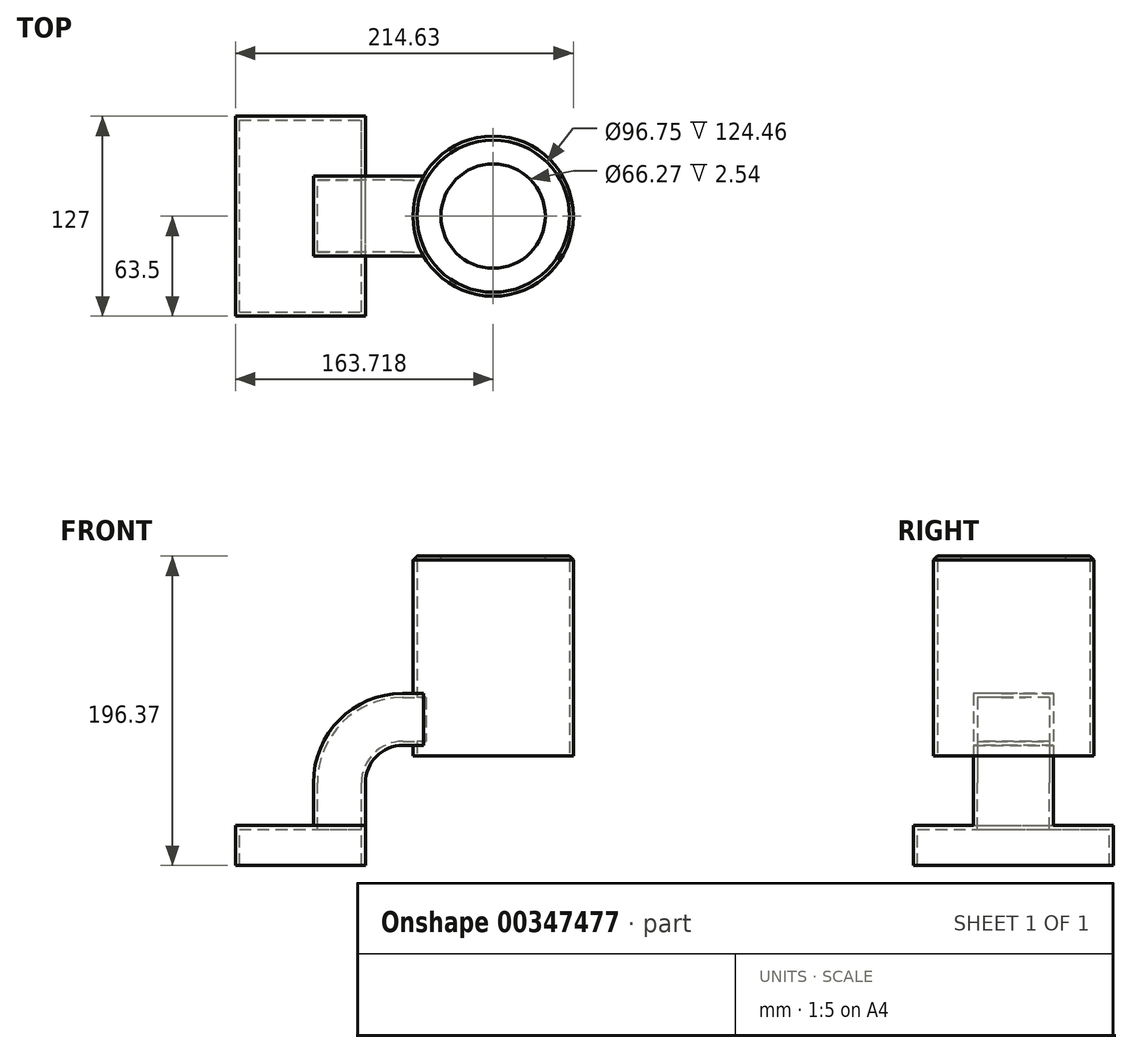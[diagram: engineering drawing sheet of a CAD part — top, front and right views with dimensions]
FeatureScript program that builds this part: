
annotation { "Feature Type Name" : "Feature", "Feature Type Description" : "" }
export const myFeature = defineFeature(function(context is Context, id is Id, definition is map)
    precondition{}
    {
        {
            var Q0;
            Q0=qCreatedBy(makeId("Front.planeOp"),FACE);
            var sketch = newSketch(context, id + "F0", { "sketchPlane" : qUnion([Q0])});
            skLineSegment(sketch, "E0.bottom", {"start": v(-41.65, -6.6) * mm, "end": v(40.9, -6.6) * mm});
            skLineSegment(sketch, "E0.top", {"start": v(-41.65, 18.8) * mm, "end": v(40.9, 18.8) * mm});
            skLineSegment(sketch, "E0.left", {"start": v(-41.65, -6.6) * mm, "end": v(-41.65, 18.8) * mm});
            skLineSegment(sketch, "E0.right", {"start": v(40.9, -6.6) * mm, "end": v(40.9, 18.8) * mm});
            skLineSegment(sketch, "E1.bottom", {"start": v(71.38, 62.77) * mm, "end": v(172.98, 62.77) * mm});
            skLineSegment(sketch, "E1.top", {"start": v(71.38, 189.77) * mm, "end": v(172.98, 189.77) * mm});
            skLineSegment(sketch, "E1.left", {"start": v(71.38, 62.77) * mm, "end": v(71.38, 189.77) * mm});
            skLineSegment(sketch, "E1.right", {"start": v(172.98, 62.77) * mm, "end": v(172.98, 189.77) * mm});
            skLineSegment(sketch, "E2", {"start": v(40.9, 18.8) * mm, "end": v(40.9, 45.75) * mm});
            skArc(sketch, "E3", {"start": v(40.9, 45.75) * mm, "mid": v(47.89, 62.61) * mm, "end": v(64.75, 69.6) * mm});
            skLineSegment(sketch, "E4", {"start": v(64.75, 69.6) * mm, "end": v(122.07, 69.6) * mm});
            skLineSegment(sketch, "E5.0", {"start": v(64.75, 102.62) * mm, "end": v(122.07, 102.62) * mm});
            skArc(sketch, "E5.1", {"start": v(7.88, 45.75) * mm, "mid": v(24.54, 85.96) * mm, "end": v(64.75, 102.62) * mm});
            skLineSegment(sketch, "E5.2", {"start": v(7.88, 18.8) * mm, "end": v(7.88, 45.75) * mm});
            skLineSegment(sketch, "E6", {"start": v(122.07, 69.6) * mm, "end": v(122.07, 102.62) * mm});
            skFitSpline(sketch, "E7", {"points": [v(-41.65, 18.8) * mm, v(64.75, 102.62) * mm], "startDerivative": vector(-1.45, 45.26) * mm, "endDerivative": vector(278.29, 0.6) * mm});
            skLineSegment(sketch, "E8", {"start": v(122.07, 62.77) * mm, "end": v(122.07, 189.77) * mm});
            skSolve(sketch);
        }
        {
            var Q0;
            Q0=makeQuery(id+"F0.imprint","IMPRINT",FACE,{"disambiguationData":[TD([[makeQuery(id+"F0.imprint","IMPRINT",EDGE,{"derivedFrom":sQuery(id+"F0.wireOp",EDGE,"E0.bottom")}),1.0]])]});
            extrude(context, id + "F1", {"entities" : qUnion([Q0]), "endBound" : BoundingType.SYMMETRIC, "depth" : 127 * mm});
        }
        {
            var Q0;
            {var subQ0=sQuery(id+"F0.wireOp",EDGE,"E2");Q0=makeQuery(id+"F0.imprint","IMPRINT",FACE,{"disambiguationData":[TD([[makeQuery(id+"F0.imprint","IMPRINT",EDGE,{"derivedFrom":subQ0}),1.0]])]});}
            var Q1;
            {var subQ5=sQuery(id+"F0.wireOp",EDGE,"E6");Q1=makeQuery(id+"F0.imprint","IMPRINT",FACE,{"disambiguationData":[TD([[makeQuery(id+"F0.imprint","IMPRINT",EDGE,{"derivedFrom":subQ5}),1.0]])]});}
            var Q2;
            {var subQ0=sQuery(id+"F0.wireOp",EDGE,"E4");var subQ1=sQuery(id+"F0.wireOp",EDGE,"E1.left");var subQ2=makeQuery(id+"F0.imprint","INTERSECT",VERTEX,{"derivedFrom":[subQ1,subQ0]});Q2=makeQuery(id+"F0.imprint","IMPRINT",FACE,{"disambiguationData":[TD([[makeQuery(id+"F0.imprint","IMPRINT",EDGE,{"disambiguationData":[TD([[subQ2,-1.0]])],"derivedFrom":subQ1}),-1.0]])]});}
            extrude(context, id + "F2", {"entities" : qUnion([Q0, Q1, Q2]), "operationType" : NewBodyOperationType.ADD, "endBound" : BoundingType.SYMMETRIC, "depth" : 50.8 * mm});
        }
        {
            var Q0;
            {var subQ4=sQuery(id+"F0.wireOp",EDGE,"E5.1");Q0=makeQuery(id+"F0.imprint","IMPRINT",FACE,{"disambiguationData":[TD([[makeQuery(id+"F0.imprint","IMPRINT",EDGE,{"derivedFrom":subQ4}),1.0]])]});}
            extrude(context, id + "F3", {"entities" : qUnion([Q0]), "operationType" : NewBodyOperationType.ADD, "endBound" : BoundingType.SYMMETRIC, "depth" : 15.24 * mm});
        }
        {
            var Q0;
            {var subQ0=sQuery(id+"F0.wireOp",EDGE,"E1.right");Q0=makeQuery(id+"F0.imprint","IMPRINT",FACE,{"disambiguationData":[TD([[makeQuery(id+"F0.imprint","IMPRINT",EDGE,{"derivedFrom":subQ0}),1.0]])]});}
            var Q1;
            Q1=sQuery(id+"F0.wireOp",EDGE,"E8");
            revolve(context, id + "F4", {"operationType" : NewBodyOperationType.ADD, "entities" : qUnion([Q0]), "axis" : qUnion([Q1]), "revolveType" : RevolveType.FULL});
        }
        {
            var Q0;
            Q0=makeQuery(id+"F1.opExtrude","SWEPT_FACE",FACE,{"disambiguationData":[OSD([sQuery(id+"F0.wireOp",EDGE,"E0.bottom")])]});
            var Q1;
            Q1=makeQuery(id+"F4.opRevolve","SWEPT_FACE",FACE,{"disambiguationData":[OSD([sQuery(id+"F0.wireOp",EDGE,"E1.bottom")])]});
            shell(context, id + "F5", {"entities" : qUnion([Q0, Q1]), "thickness" : 2.54 * mm});
        }
        {
            var Q0;
            Q0=makeQuery(id+"F4.opRevolve","SWEPT_EDGE",EDGE,{"disambiguationData":[OSD([sQuery(id+"F0.wireOp",EDGE,"E1.top"),sQuery(id+"F0.wireOp",EDGE,"E1.right")])]});
            chamfer(context, id + "F6", {"entities" : qUnion([Q0]), "width" : 2.54 * mm, "tangentPropagation" : true});
        }
        {
            var Q0;
            Q0=makeQuery(id+"F4.opRevolve","SWEPT_FACE",FACE,{"disambiguationData":[OSD([sQuery(id+"F0.wireOp",EDGE,"E1.top")])]});
            var sketch = newSketch(context, id + "F7", { "sketchPlane" : qUnion([Q0])});
            skCircle(sketch, "E9", {"center": v(122.07, 0) * mm, "radius": 33.14 * mm});
            skSolve(sketch);
        }
        {
            var Q0;
            Q0=makeQuery(id+"F7.imprint","IMPRINT",FACE,{"disambiguationData":[TD([[makeQuery(id+"F7.imprint","IMPRINT",EDGE,{"derivedFrom":sQuery(id+"F7.wireOp",EDGE,"E9")}),1.0]])]});
            extrude(context, id + "F8", {"entities" : qUnion([Q0]), "operationType" : NewBodyOperationType.REMOVE, "endBound" : BoundingType.THROUGH_ALL, "oppositeDirection" : true, "depth" : 25.4 * mm});
        }
    });
